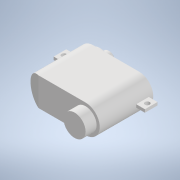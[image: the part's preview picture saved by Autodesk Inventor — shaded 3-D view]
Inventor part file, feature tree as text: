
AUTODESK INVENTOR PART (.ipt)
format: ipt  version: 2022 (Build 260153000, 153)  size: 177,152 bytes
history: native  units: mm
features: extrude x6, sketch x6, other x1, fillet x1, chamfer x1
ambient origin geometry x8: Origin, YZ Plane, XZ Plane, XY Plane, X Axis, Y Axis, Z Axis, Center Point
bodies: Body1 (feature_tree)
feature tree (15):
  other  "Твердое тело1"
  extrude  "Выдавливание1"  Depth=23.5mm
  extrude  "Выдавливание2"  Depth=9.0mm
  fillet  "Сопряжение1"  Radius=17.0mm
  extrude  "Выдавливание3"  Depth=29.0mm
  extrude  "Выдавливание4"  Depth=4.0mm
  extrude  "Выдавливание5"  Depth=26.5mm
  extrude  "Выдавливание6"  Depth=1.5mm
  chamfer  "Фаска1"  Distance=1.5mm
  sketch  "Эскиз1"
  sketch  "Эскиз2"
  sketch  "Эскиз3"
  sketch  "Эскиз4"
  sketch  "Эскиз5"
  sketch  "Эскиз6"
